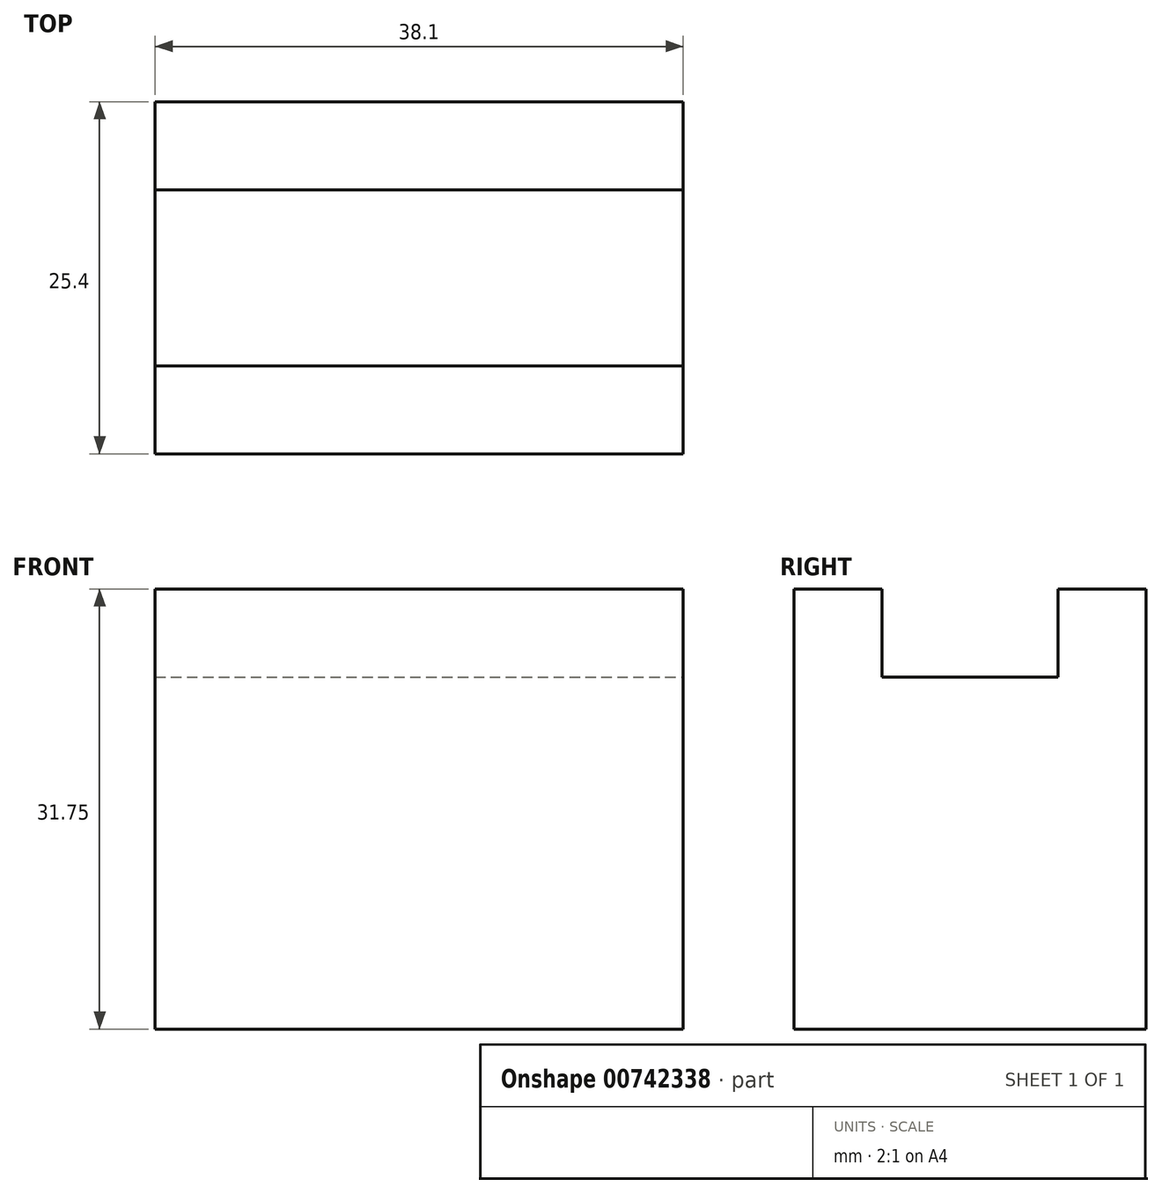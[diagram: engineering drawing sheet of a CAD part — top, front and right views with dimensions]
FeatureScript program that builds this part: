
annotation { "Feature Type Name" : "Feature", "Feature Type Description" : "" }
export const myFeature = defineFeature(function(context is Context, id is Id, definition is map)
    precondition{}
    {
        {
            var Q0;
            Q0=qCreatedBy(makeId("Right.planeOp"),FACE);
            var sketch = newSketch(context, id + "F0", { "sketchPlane" : qUnion([Q0])});
            skLineSegment(sketch, "E0", {"start": v(0, 0) * mm, "end": v(-25.4, 0) * mm});
            skLineSegment(sketch, "E1", {"start": v(-25.4, 0) * mm, "end": v(-25.4, 31.75) * mm});
            skLineSegment(sketch, "E2", {"start": v(-25.4, 31.75) * mm, "end": v(0, 31.75) * mm});
            skLineSegment(sketch, "E3", {"start": v(0, 31.75) * mm, "end": v(0, 0) * mm});
            skSolve(sketch);
        }
        {
            var Q0;
            Q0 = qSketchRegion(id + "F0", true);
            extrude(context, id + "F1", {"entities" : qUnion([Q0]), "depth" : 38.1 * mm, "offsetDistance" : 25.4 * mm});
        }
        {
            var Q0;
            Q0=makeQuery(id+"F1.opExtrude","CAP_FACE",FACE,{"disambiguationData":[OSD([sQuery(id+"F0.wireOp",EDGE,"E0"),sQuery(id+"F0.wireOp",EDGE,"E1"),sQuery(id+"F0.wireOp",EDGE,"E2"),sQuery(id+"F0.wireOp",EDGE,"E3")])],"isStart":false});
            var sketch = newSketch(context, id + "F2", { "sketchPlane" : qUnion([Q0])});
            skLineSegment(sketch, "E4", {"start": v(-19.05, 31.75) * mm, "end": v(-19.05, 25.4) * mm});
            skLineSegment(sketch, "E5", {"start": v(-19.05, 25.4) * mm, "end": v(-6.35, 25.4) * mm});
            skLineSegment(sketch, "E6", {"start": v(-6.35, 25.4) * mm, "end": v(-6.35, 31.75) * mm});
            skLineSegment(sketch, "E7", {"start": v(-6.35, 31.75) * mm, "end": v(-19.05, 31.75) * mm});
            skLineSegment(sketch, "E8", {"start": v(-19.05, 31.75) * mm, "end": v(-25.4, 31.75) * mm});
            skSolve(sketch);
        }
        {
            var Q0;
            Q0=makeQuery(id+"F2.imprint","IMPRINT",FACE,{"disambiguationData":[TD([[makeQuery(id+"F2.imprint","IMPRINT",EDGE,{"derivedFrom":sQuery(id+"F2.wireOp",EDGE,"E4")}),1.0]])]});
            extrude(context, id + "F3", {"entities" : qUnion([Q0]), "operationType" : NewBodyOperationType.REMOVE, "endBound" : BoundingType.THROUGH_ALL, "oppositeDirection" : true, "depth" : 25.4 * mm, "offsetDistance" : 25.4 * mm});
        }
        {
            var Q0;
            Q0 = qSketchRegion(id + "F2", true);
            extrude(context, id + "F4", {"entities" : qUnion([Q0]), "operationType" : NewBodyOperationType.REMOVE, "endBound" : BoundingType.THROUGH_ALL, "oppositeDirection" : true, "depth" : 25.4 * mm, "offsetDistance" : 25.4 * mm});
        }
    });
